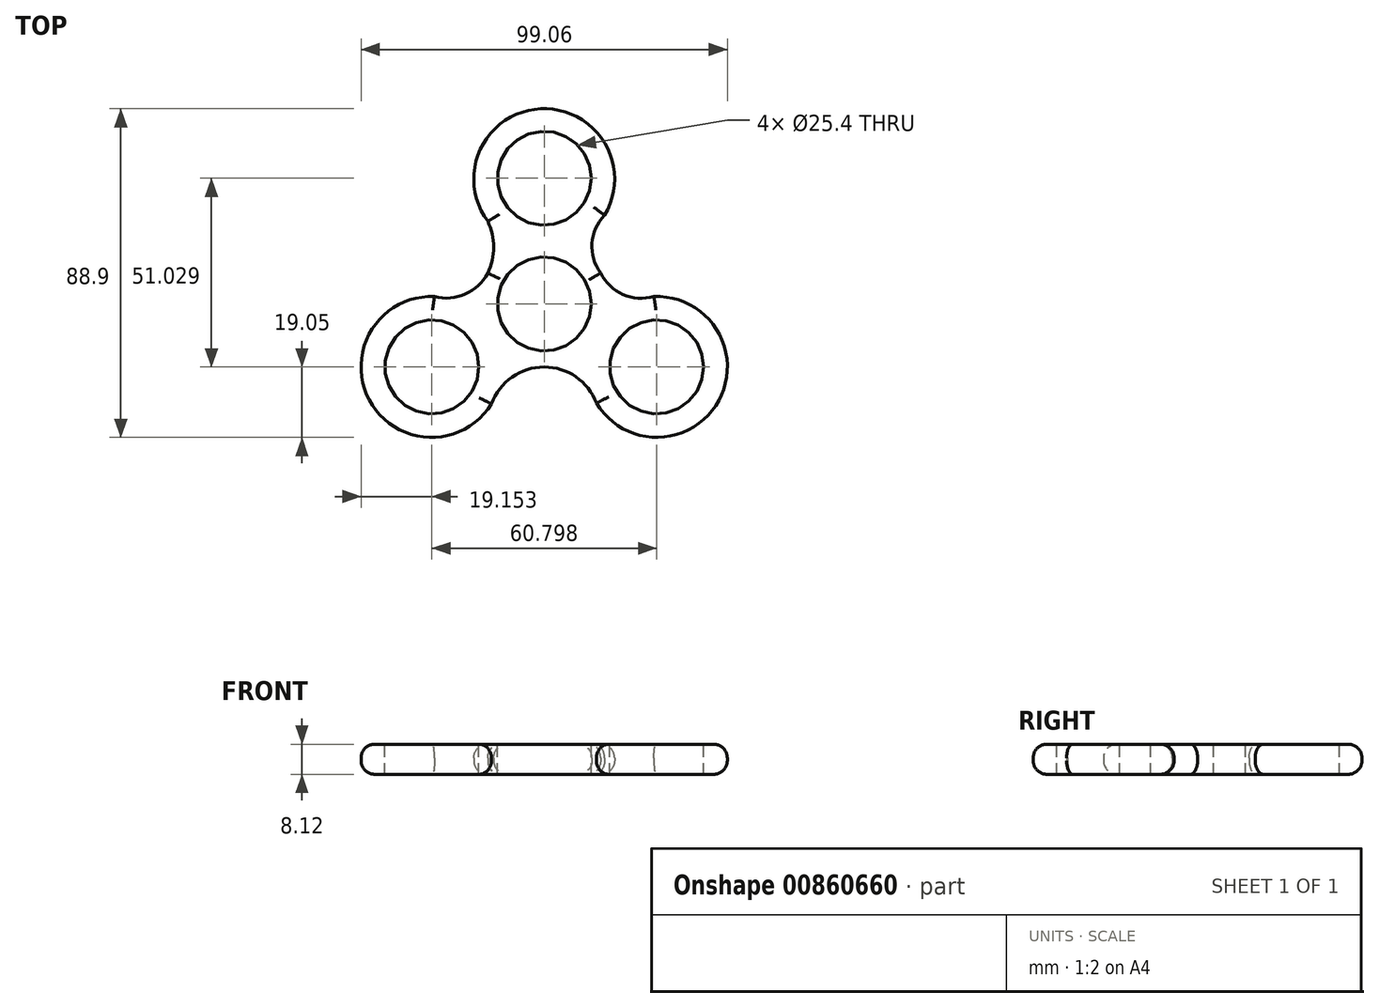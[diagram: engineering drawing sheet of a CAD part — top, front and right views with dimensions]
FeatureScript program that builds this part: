
annotation { "Feature Type Name" : "Feature", "Feature Type Description" : "" }
export const myFeature = defineFeature(function(context is Context, id is Id, definition is map)
    precondition{}
    {
        {
            var Q0;
            Q0=qCreatedBy(makeId("Top.planeOp"),FACE);
            var sketch = newSketch(context, id + "F0", { "sketchPlane" : qUnion([Q0])});
            skLineSegment(sketch, "E0", {"start": v(0, 0) * mm, "end": v(0, 50.8) * mm});
            skLineSegment(sketch, "E1", {"start": v(0, 0) * mm, "end": v(30.48, 0) * mm});
            skLineSegment(sketch, "E2", {"start": v(0, 0) * mm, "end": v(-30.48, 0) * mm});
            skLineSegment(sketch, "E3", {"start": v(0, 50.8) * mm, "end": v(-30.48, 0) * mm});
            skLineSegment(sketch, "E4", {"start": v(0, 50.8) * mm, "end": v(30.48, 0) * mm});
            skLineSegment(sketch, "E5", {"start": v(-30.48, 0) * mm, "end": v(30.48, 0) * mm});
            skCircle(sketch, "E6", {"center": v(0, 50.8) * mm, "radius": 19.05 * mm});
            skCircle(sketch, "E7", {"center": v(-30.48, 0) * mm, "radius": 19.05 * mm});
            skCircle(sketch, "E8", {"center": v(30.48, 0) * mm, "radius": 19.05 * mm});
            skArc(sketch, "E9", {"start": v(0, 0) * mm, "mid": v(-8.7, -2.75) * mm, "end": v(-14.26, -10) * mm});
            skArc(sketch, "E10", {"start": v(14.12, -9.76) * mm, "mid": v(8.58, -2.68) * mm, "end": v(0, 0) * mm});
            skArc(sketch, "E11", {"start": v(15.24, 25.4) * mm, "mid": v(21.31, 19.63) * mm, "end": v(29.67, 19.03) * mm});
            skArc(sketch, "E12", {"start": v(16.34, 41) * mm, "mid": v(12.94, 33.4) * mm, "end": v(15.24, 25.4) * mm});
            skArc(sketch, "E13", {"start": v(-29.67, 19.03) * mm, "mid": v(-21.34, 19.7) * mm, "end": v(-15.24, 25.4) * mm});
            skArc(sketch, "E14", {"start": v(-15.24, 25.4) * mm, "mid": v(-13.67, 32.39) * mm, "end": v(-15.24, 39.37) * mm});
            skSolve(sketch);
        }
        {
            var Q0;
            {var subQ1=sQuery(id+"F0.wireOp",EDGE,"E7");var subQ5=sQuery(id+"F0.wireOp",EDGE,"E2");var subQ6=makeQuery(id+"F0.imprint","INTERSECT",VERTEX,{"derivedFrom":[subQ5,subQ1]});Q0=makeQuery(id+"F0.imprint","IMPRINT",FACE,{"disambiguationData":[TD([[makeQuery(id+"F0.imprint","IMPRINT",EDGE,{"disambiguationData":[TD([[subQ6,-1.0]])],"derivedFrom":subQ5}),1.0]])]});}
            var Q1;
            {var subQ0=sQuery(id+"F0.wireOp",EDGE,"E7");var subQ1=sQuery(id+"F0.wireOp",EDGE,"E2");var subQ2=makeQuery(id+"F0.imprint","INTERSECT",VERTEX,{"derivedFrom":[subQ1,subQ0]});Q1=makeQuery(id+"F0.imprint","IMPRINT",FACE,{"disambiguationData":[TD([[makeQuery(id+"F0.imprint","IMPRINT",EDGE,{"disambiguationData":[TD([[subQ2,-1.0]])],"derivedFrom":subQ1}),-1.0]])]});}
            var Q2;
            {var subQ0=sQuery(id+"F0.wireOp",EDGE,"E7");var subQ1=sQuery(id+"F0.wireOp",EDGE,"E3");var subQ2=makeQuery(id+"F0.imprint","INTERSECT",VERTEX,{"derivedFrom":[subQ1,subQ0]});Q2=makeQuery(id+"F0.imprint","IMPRINT",FACE,{"disambiguationData":[TD([[makeQuery(id+"F0.imprint","IMPRINT",EDGE,{"disambiguationData":[TD([[subQ2,1.0]])],"derivedFrom":subQ1}),-1.0]])]});}
            var Q3;
            {var subQ0=sQuery(id+"F0.wireOp",EDGE,"E7");var subQ1=sQuery(id+"F0.wireOp",EDGE,"E3");var subQ2=makeQuery(id+"F0.imprint","INTERSECT",VERTEX,{"derivedFrom":[subQ1,subQ0]});Q3=makeQuery(id+"F0.imprint","IMPRINT",FACE,{"disambiguationData":[TD([[makeQuery(id+"F0.imprint","IMPRINT",EDGE,{"disambiguationData":[TD([[subQ2,1.0]])],"derivedFrom":subQ1}),1.0]])]});}
            var Q4;
            {var subQ1=sQuery(id+"F0.wireOp",EDGE,"E2");var subQ3=sQuery(id+"F0.wireOp",EDGE,"E7");var subQ4=makeQuery(id+"F0.imprint","INTERSECT",VERTEX,{"derivedFrom":[subQ1,subQ3]});Q4=makeQuery(id+"F0.imprint","IMPRINT",FACE,{"disambiguationData":[TD([[makeQuery(id+"F0.imprint","IMPRINT",EDGE,{"disambiguationData":[TD([[subQ4,1.0]])],"derivedFrom":subQ3}),-1.0]])]});}
            var Q5;
            {var subQ1=sQuery(id+"F0.wireOp",EDGE,"E4");var subQ10=sQuery(id+"F0.wireOp",EDGE,"E11");var subQ11=makeQuery(id+"F0.imprint","INTERSECT",VERTEX,{"derivedFrom":[subQ1,subQ10]});Q5=makeQuery(id+"F0.imprint","IMPRINT",FACE,{"disambiguationData":[TD([[makeQuery(id+"F0.imprint","IMPRINT",EDGE,{"disambiguationData":[TD([[subQ11,-1.0]])],"derivedFrom":subQ1}),-1.0]])]});}
            var Q6;
            {var subQ0=sQuery(id+"F0.wireOp",EDGE,"E14");Q6=makeQuery(id+"F0.imprint","IMPRINT",FACE,{"disambiguationData":[TD([[makeQuery(id+"F0.imprint","IMPRINT",EDGE,{"derivedFrom":subQ0}),-1.0]])]});}
            var Q7;
            {var subQ1=sQuery(id+"F0.wireOp",EDGE,"E6");var subQ8=makeQuery(id+"F0.imprint","INTERSECT",VERTEX,{"derivedFrom":[subQ1,sQuery(id+"F0.wireOp",EDGE,"E14")]});Q7=makeQuery(id+"F0.imprint","IMPRINT",FACE,{"disambiguationData":[TD([[makeQuery(id+"F0.imprint","IMPRINT",EDGE,{"disambiguationData":[TD([[subQ8,-1.0]])],"derivedFrom":subQ1}),1.0]])]});}
            var Q8;
            {var subQ1=sQuery(id+"F0.wireOp",EDGE,"E0");var subQ3=sQuery(id+"F0.wireOp",EDGE,"E6");var subQ4=makeQuery(id+"F0.imprint","INTERSECT",VERTEX,{"derivedFrom":[subQ1,subQ3]});Q8=makeQuery(id+"F0.imprint","IMPRINT",FACE,{"disambiguationData":[TD([[makeQuery(id+"F0.imprint","IMPRINT",EDGE,{"disambiguationData":[TD([[subQ4,1.0]])],"derivedFrom":subQ3}),1.0]])]});}
            var Q9;
            {var subQ1=sQuery(id+"F0.wireOp",EDGE,"E0");var subQ3=sQuery(id+"F0.wireOp",EDGE,"E6");var subQ4=makeQuery(id+"F0.imprint","INTERSECT",VERTEX,{"derivedFrom":[subQ1,subQ3]});Q9=makeQuery(id+"F0.imprint","IMPRINT",FACE,{"disambiguationData":[TD([[makeQuery(id+"F0.imprint","IMPRINT",EDGE,{"disambiguationData":[TD([[subQ4,-1.0]])],"derivedFrom":subQ3}),1.0]])]});}
            var Q10;
            {var subQ0=sQuery(id+"F0.wireOp",EDGE,"E8");var subQ1=sQuery(id+"F0.wireOp",EDGE,"E1");var subQ2=makeQuery(id+"F0.imprint","INTERSECT",VERTEX,{"derivedFrom":[subQ1,subQ0]});Q10=makeQuery(id+"F0.imprint","IMPRINT",FACE,{"disambiguationData":[TD([[makeQuery(id+"F0.imprint","IMPRINT",EDGE,{"disambiguationData":[TD([[subQ2,-1.0]])],"derivedFrom":subQ1}),1.0]])]});}
            var Q11;
            {var subQ1=sQuery(id+"F0.wireOp",EDGE,"E8");var subQ6=sQuery(id+"F0.wireOp",EDGE,"E1");var subQ7=makeQuery(id+"F0.imprint","INTERSECT",VERTEX,{"derivedFrom":[subQ6,subQ1]});Q11=makeQuery(id+"F0.imprint","IMPRINT",FACE,{"disambiguationData":[TD([[makeQuery(id+"F0.imprint","IMPRINT",EDGE,{"disambiguationData":[TD([[subQ7,-1.0]])],"derivedFrom":subQ6}),-1.0]])]});}
            var Q12;
            {var subQ1=sQuery(id+"F0.wireOp",EDGE,"E1");var subQ3=sQuery(id+"F0.wireOp",EDGE,"E8");var subQ4=makeQuery(id+"F0.imprint","INTERSECT",VERTEX,{"derivedFrom":[subQ1,subQ3]});Q12=makeQuery(id+"F0.imprint","IMPRINT",FACE,{"disambiguationData":[TD([[makeQuery(id+"F0.imprint","IMPRINT",EDGE,{"disambiguationData":[TD([[subQ4,-1.0]])],"derivedFrom":subQ3}),-1.0]])]});}
            var Q13;
            {var subQ0=sQuery(id+"F0.wireOp",EDGE,"E11");var subQ1=sQuery(id+"F0.wireOp",EDGE,"E4");var subQ2=makeQuery(id+"F0.imprint","INTERSECT",VERTEX,{"derivedFrom":[subQ1,subQ0]});Q13=makeQuery(id+"F0.imprint","IMPRINT",FACE,{"disambiguationData":[TD([[makeQuery(id+"F0.imprint","IMPRINT",EDGE,{"disambiguationData":[TD([[subQ2,-1.0]])],"derivedFrom":subQ1}),1.0]])]});}
            var Q14;
            {var subQ0=sQuery(id+"F0.wireOp",EDGE,"E12");var subQ1=sQuery(id+"F0.wireOp",EDGE,"E4");var subQ2=makeQuery(id+"F0.imprint","INTERSECT",VERTEX,{"derivedFrom":[subQ1,subQ0]});Q14=makeQuery(id+"F0.imprint","IMPRINT",FACE,{"disambiguationData":[TD([[makeQuery(id+"F0.imprint","IMPRINT",EDGE,{"disambiguationData":[TD([[subQ2,1.0]])],"derivedFrom":subQ1}),1.0]])]});}
            extrude(context, id + "F1", {"entities" : qUnion([Q0, Q1, Q2, Q3, Q4, Q5, Q6, Q7, Q8, Q9, Q10, Q11, Q12, Q13, Q14]), "endBound" : BoundingType.SYMMETRIC, "depth" : 8.13 * mm, "offsetDistance" : 25.4 * mm});
        }
        {
            var Q0;
            Q0=makeQuery(id+"F1.opExtrude","CAP_FACE",FACE,{"disambiguationData":[OSD([sQuery(id+"F0.wireOp",EDGE,"E6"),sQuery(id+"F0.wireOp",EDGE,"E7"),sQuery(id+"F0.wireOp",EDGE,"E8"),sQuery(id+"F0.wireOp",EDGE,"E9"),sQuery(id+"F0.wireOp",EDGE,"E10"),sQuery(id+"F0.wireOp",EDGE,"E11"),sQuery(id+"F0.wireOp",EDGE,"E12"),sQuery(id+"F0.wireOp",EDGE,"E13"),sQuery(id+"F0.wireOp",EDGE,"E14")])],"isStart":false});
            var Q1;
            Q1=makeQuery(id+"F1.opExtrude","CAP_FACE",FACE,{"disambiguationData":[OSD([sQuery(id+"F0.wireOp",EDGE,"E6"),sQuery(id+"F0.wireOp",EDGE,"E7"),sQuery(id+"F0.wireOp",EDGE,"E8"),sQuery(id+"F0.wireOp",EDGE,"E9"),sQuery(id+"F0.wireOp",EDGE,"E10"),sQuery(id+"F0.wireOp",EDGE,"E11"),sQuery(id+"F0.wireOp",EDGE,"E12"),sQuery(id+"F0.wireOp",EDGE,"E13"),sQuery(id+"F0.wireOp",EDGE,"E14")])],"isStart":true});
            fillet(context, id + "F2", {"entities" : qUnion([Q0, Q1]), "radius" : 3.68 * mm, "tangentPropagation" : true, "allowEdgeOverflow" : false});
        }
        {
            var Q0;
            Q0=qCreatedBy(makeId("Top.planeOp"),FACE);
            cPlane(context, id + "F3", {"entities" : qUnion([Q0]), "cplaneType" : CPlaneType.OFFSET, "offset" : 4.06 * mm, "width" : 152.4 * mm, "height" : 152.4 * mm});
        }
        {
            var Q0;
            Q0=qCreatedBy(id+"F3.planeOp",FACE);
            var sketch = newSketch(context, id + "F4", { "sketchPlane" : qUnion([Q0])});
            skLineSegment(sketch, "E15", {"start": v(0, 51.03) * mm, "end": v(30.42, 0) * mm});
            skLineSegment(sketch, "E16", {"start": v(30.42, 0) * mm, "end": v(-30.38, 0) * mm});
            skLineSegment(sketch, "E17", {"start": v(-30.38, 0) * mm, "end": v(0, 51.03) * mm});
            skLineSegment(sketch, "E18", {"start": v(0, 51.03) * mm, "end": v(0, 0) * mm});
            skLineSegment(sketch, "E19", {"start": v(0, 0) * mm, "end": v(-30.38, 0) * mm});
            skLineSegment(sketch, "E20", {"start": v(-30.38, 0) * mm, "end": v(15.21, 25.51) * mm});
            skLineSegment(sketch, "E21", {"start": v(15.21, 25.51) * mm, "end": v(30.42, 0) * mm});
            skLineSegment(sketch, "E22", {"start": v(30.42, 0) * mm, "end": v(-15.19, 25.51) * mm});
            skLineSegment(sketch, "E23", {"start": v(0, 0) * mm, "end": v(0, 17.02) * mm});
            skLineSegment(sketch, "E24", {"start": v(0, 17.02) * mm, "end": v(0, 0) * mm});
            skSolve(sketch);
        }
        {
            var Q0;
            Q0=sQuery(id+"F4.wireOp",VERTEX,"E15.end");
            var Q1;
            Q1=sQuery(id+"F4.wireOp",VERTEX,"E15.start");
            var Q2;
            Q2=sQuery(id+"F4.wireOp",VERTEX,"E16.end");
            var Q3;
            Q3=makeQuery(id+"F1.opExtrude","SWEPT_BODY",BODY,{"disambiguationData":[OSD([sQuery(id+"F0.wireOp",EDGE,"E6"),sQuery(id+"F0.wireOp",EDGE,"E7"),sQuery(id+"F0.wireOp",EDGE,"E8"),sQuery(id+"F0.wireOp",EDGE,"E9"),sQuery(id+"F0.wireOp",EDGE,"E10"),sQuery(id+"F0.wireOp",EDGE,"E11"),sQuery(id+"F0.wireOp",EDGE,"E12"),sQuery(id+"F0.wireOp",EDGE,"E13"),sQuery(id+"F0.wireOp",EDGE,"E14")])]});
            hole(context, id + "F5", {"style" : HoleStyle.SIMPLE, "endStyle" : HoleEndStyle.THROUGH, "holeDiameter" : 25.4 * mm, "majorDiameter" : 6.35 * mm, "isTappedThrough" : true, "tappedDepth" : 12.7 * mm, "tapClearance" : 3, "locations" : qUnion([Q0, Q1, Q2]), "scope" : qUnion([Q3])});
        }
        {
            var Q0;
            Q0=sQuery(id+"F4.wireOp",VERTEX,"E23.end");
            var Q1;
            Q1=makeQuery(id+"F1.opExtrude","SWEPT_BODY",BODY,{"disambiguationData":[OSD([sQuery(id+"F0.wireOp",EDGE,"E6"),sQuery(id+"F0.wireOp",EDGE,"E7"),sQuery(id+"F0.wireOp",EDGE,"E8"),sQuery(id+"F0.wireOp",EDGE,"E9"),sQuery(id+"F0.wireOp",EDGE,"E10"),sQuery(id+"F0.wireOp",EDGE,"E11"),sQuery(id+"F0.wireOp",EDGE,"E12"),sQuery(id+"F0.wireOp",EDGE,"E13"),sQuery(id+"F0.wireOp",EDGE,"E14")])]});
            hole(context, id + "F6", {"style" : HoleStyle.SIMPLE, "endStyle" : HoleEndStyle.THROUGH, "holeDiameter" : 25.4 * mm, "majorDiameter" : 6.35 * mm, "isTappedThrough" : true, "tappedDepth" : 12.7 * mm, "tapClearance" : 3, "locations" : qUnion([Q0]), "scope" : qUnion([Q1])});
        }
    });
